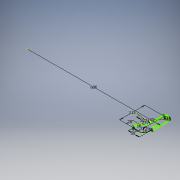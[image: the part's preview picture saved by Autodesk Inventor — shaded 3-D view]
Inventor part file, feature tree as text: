
AUTODESK INVENTOR PART (.ipt)
format: ipt  version: 2019.2 (Build 232265000, 265)  size: 245,248 bytes
history: native  units: mm
features: sketch x1
ambient origin geometry x8: Origin, YZ Plane, XZ Plane, XY Plane, X Axis, Y Axis, Z Axis, Center Point
feature tree (1):
  sketch  "Sketch1"  dims[d0=6.0mm d1=6.0mm d2=33.0mm d3=50.0mm d4=24.0mm d5=21.0mm d6=50.0mm d10=27.0mm d11=6.0mm d12=28.0mm d13=16.0mm d14=74.0mm d15=15.0mm d16=115.0mm d17=25.0mm d18=32.0mm d19=19.0mm d20=7.5mm d21=600.0mm]
